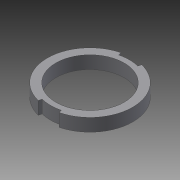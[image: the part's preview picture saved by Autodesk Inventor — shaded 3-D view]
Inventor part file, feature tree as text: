
AUTODESK INVENTOR PART (.ipt)
format: ipt  version: 2016 (Build 200138000, 138)  size: 100,352 bytes
history: native  units: mm
features: extrude x2, sketch x2
ambient origin geometry x8: Origin, YZ Plane, XZ Plane, XY Plane, X Axis, Y Axis, Z Axis, Center Point
bodies: Solid1 (feature_tree)
feature tree (4):
  extrude  "Extrusion1"  Depth=40.0mm
  extrude  "Extrusion2"  Depth=6.0mm
  sketch  "Sketch1"  dims[d0=32.0mm d1=40.0mm]
  sketch  "Sketch2"  dims[d2=6.0mm d3=0.0mm d4=9.0mm d5=1.5mm d6=6.0mm d7=0.0mm]
